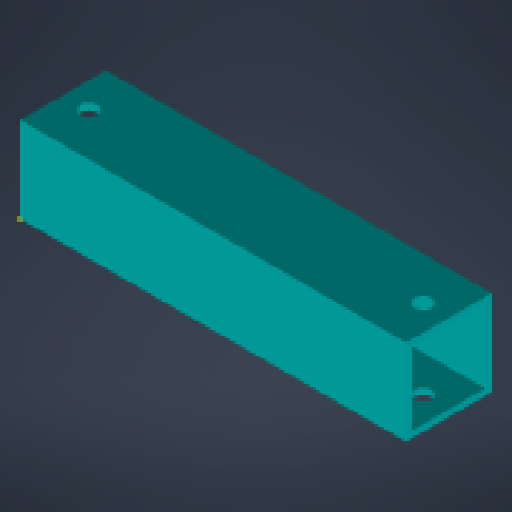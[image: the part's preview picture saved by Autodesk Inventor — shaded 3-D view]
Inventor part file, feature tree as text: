
AUTODESK INVENTOR PART (.ipt)
format: ipt  version: 2024 (Build 280153000, 153)  size: 148,992 bytes
history: native  units: mm
features: extrude x2, sketch x2, other x1
ambient origin geometry x8: Origin, YZ Plane, XZ Plane, XY Plane, X Axis, Y Axis, Z Axis, Center Point
bodies: Body1 (feature_tree)
feature tree (5):
  other  "Твердое тело1"
  extrude  "Выдавливание1"  Depth=20.0mm
  extrude  "Выдавливание2"  Depth=1.5mm
  sketch  "Эскиз2"
  sketch  "Эскиз3"
